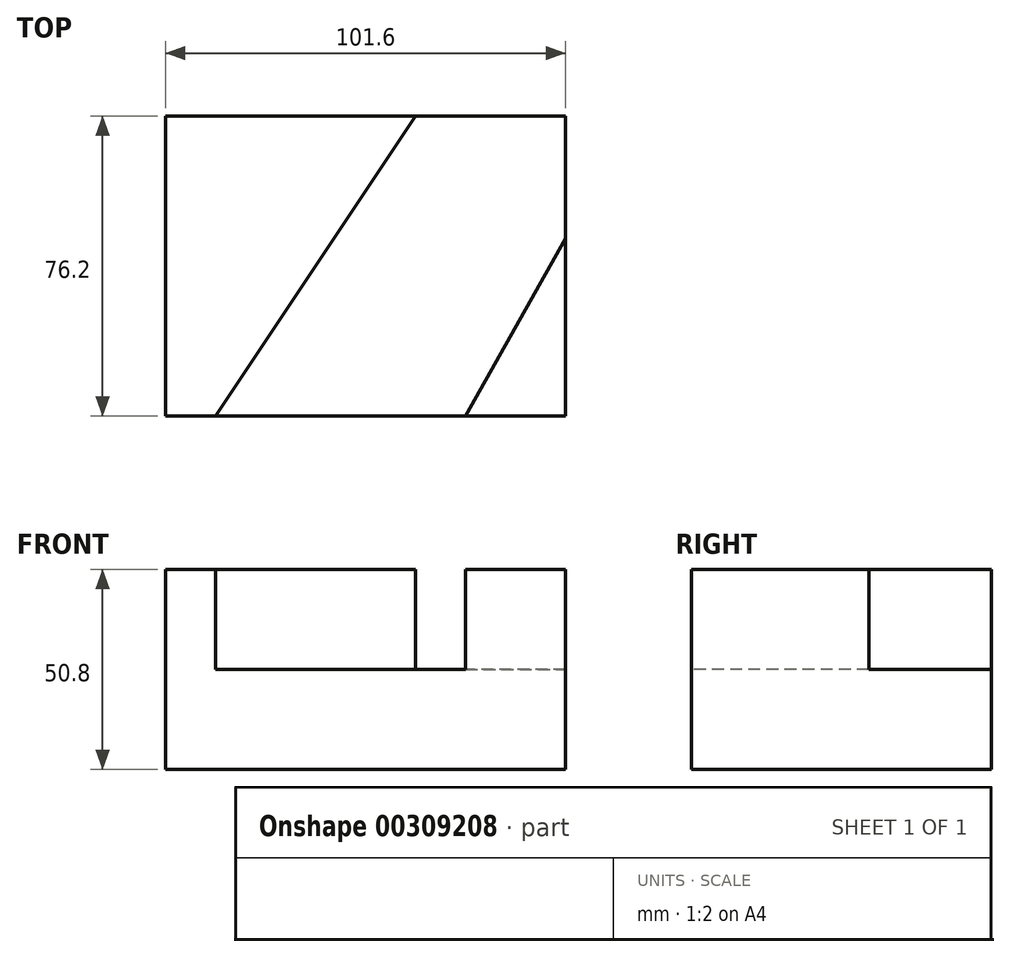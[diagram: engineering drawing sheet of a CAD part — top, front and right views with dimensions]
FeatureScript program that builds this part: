
annotation { "Feature Type Name" : "Feature", "Feature Type Description" : "" }
export const myFeature = defineFeature(function(context is Context, id is Id, definition is map)
    precondition{}
    {
        {
            var Q0;
            Q0=qCreatedBy(makeId("Top.planeOp"),FACE);
            var sketch = newSketch(context, id + "F0", { "sketchPlane" : qUnion([Q0])});
            skLineSegment(sketch, "E0", {"start": v(-61.1, 20.05) * mm, "end": v(-61.1, -56.15) * mm});
            skLineSegment(sketch, "E1", {"start": v(-61.1, -56.15) * mm, "end": v(40.5, -56.15) * mm});
            skLineSegment(sketch, "E2", {"start": v(40.5, -56.15) * mm, "end": v(40.5, 20.05) * mm});
            skLineSegment(sketch, "E3", {"start": v(40.5, 20.05) * mm, "end": v(-61.1, 20.05) * mm});
            skSolve(sketch);
        }
        {
            var Q0;
            Q0=makeQuery(id+"F0.imprint","IMPRINT",FACE,{"disambiguationData":[TD([[makeQuery(id+"F0.imprint","IMPRINT",EDGE,{"derivedFrom":sQuery(id+"F0.wireOp",EDGE,"E0")}),1.0]])]});
            extrude(context, id + "F1", {"entities" : qUnion([Q0]), "depth" : 25.4 * mm});
        }
        {
            var Q0;
            Q0=makeQuery(id+"F1.opExtrude","CAP_FACE",FACE,{"disambiguationData":[OSD([sQuery(id+"F0.wireOp",EDGE,"E0"),sQuery(id+"F0.wireOp",EDGE,"E1"),sQuery(id+"F0.wireOp",EDGE,"E2"),sQuery(id+"F0.wireOp",EDGE,"E3")])],"isStart":false});
            var sketch = newSketch(context, id + "F2", { "sketchPlane" : qUnion([Q0])});
            skLineSegment(sketch, "E4", {"start": v(-61.1, -68.85) * mm, "end": v(25.32, 20.05) * mm});
            skLineSegment(sketch, "E5", {"start": v(25.32, 20.05) * mm, "end": v(-61.1, 20.05) * mm});
            skLineSegment(sketch, "E6", {"start": v(-61.1, 20.05) * mm, "end": v(-61.1, -68.85) * mm});
            skSolve(sketch);
        }
        {
            var Q0;
            Q0=makeQuery(id+"F2.imprint","IMPRINT",FACE,{"disambiguationData":[TD([[makeQuery(id+"F2.imprint","IMPRINT",EDGE,{"derivedFrom":sQuery(id+"F2.wireOp",EDGE,"E4")}),1.0]])]});
            extrude(context, id + "F3", {"entities" : qUnion([Q0]), "operationType" : NewBodyOperationType.ADD, "depth" : 25.4 * mm});
        }
        {
            var Q0;
            Q0=makeQuery(id+"F1.opExtrude","CAP_FACE",FACE,{"disambiguationData":[OSD([sQuery(id+"F0.wireOp",EDGE,"E0"),sQuery(id+"F0.wireOp",EDGE,"E1"),sQuery(id+"F0.wireOp",EDGE,"E2"),sQuery(id+"F0.wireOp",EDGE,"E3")])],"isStart":false});
            var sketch = newSketch(context, id + "F4", { "sketchPlane" : qUnion([Q0])});
            skLineSegment(sketch, "E7", {"start": v(40.5, -56.15) * mm, "end": v(40.5, -11.1) * mm});
            skLineSegment(sketch, "E8", {"start": v(40.5, -56.15) * mm, "end": v(15.1, -56.15) * mm});
            skLineSegment(sketch, "E9", {"start": v(15.1, -56.15) * mm, "end": v(40.5, -11.1) * mm});
            skSolve(sketch);
        }
        {
            var Q0;
            Q0=makeQuery(id+"F4.imprint","IMPRINT",FACE,{"disambiguationData":[TD([[makeQuery(id+"F4.imprint","IMPRINT",EDGE,{"derivedFrom":sQuery(id+"F4.wireOp",EDGE,"E7")}),1.0]])]});
            extrude(context, id + "F5", {"entities" : qUnion([Q0]), "operationType" : NewBodyOperationType.ADD, "depth" : 25.4 * mm});
        }
        {
            var Q0;
            Q0=makeQuery(id+"F3.opExtrude","SWEPT_BODY",BODY,{"disambiguationData":[OSD([sQuery(id+"F0.wireOp",EDGE,"E2"),sQuery(id+"F2.wireOp",EDGE,"E4"),sQuery(id+"F2.wireOp",EDGE,"E5")])]});
            deleteBodies(context, id + "F6", {"entities" : qUnion([Q0])});
        }
        {
            var Q0;
            Q0=makeQuery(id+"F1.opExtrude","CAP_FACE",FACE,{"disambiguationData":[OSD([sQuery(id+"F0.wireOp",EDGE,"E0"),sQuery(id+"F0.wireOp",EDGE,"E1"),sQuery(id+"F0.wireOp",EDGE,"E2"),sQuery(id+"F0.wireOp",EDGE,"E3")])],"isStart":false});
            var sketch = newSketch(context, id + "F7", { "sketchPlane" : qUnion([Q0])});
            skLineSegment(sketch, "E10", {"start": v(-48.4, -56.15) * mm, "end": v(-61.1, -56.15) * mm});
            skLineSegment(sketch, "E11", {"start": v(-61.1, -56.15) * mm, "end": v(-61.1, 20.05) * mm});
            skLineSegment(sketch, "E12", {"start": v(-61.1, 20.05) * mm, "end": v(2.4, 20.05) * mm});
            skLineSegment(sketch, "E13", {"start": v(2.4, 20.05) * mm, "end": v(-48.4, -56.15) * mm});
            skSolve(sketch);
        }
        {
            var Q0;
            Q0=makeQuery(id+"F7.imprint","IMPRINT",FACE,{"disambiguationData":[TD([[makeQuery(id+"F7.imprint","IMPRINT",EDGE,{"derivedFrom":sQuery(id+"F7.wireOp",EDGE,"E10")}),1.0]])]});
            extrude(context, id + "F8", {"entities" : qUnion([Q0]), "operationType" : NewBodyOperationType.ADD, "depth" : 25.4 * mm});
        }
    });
